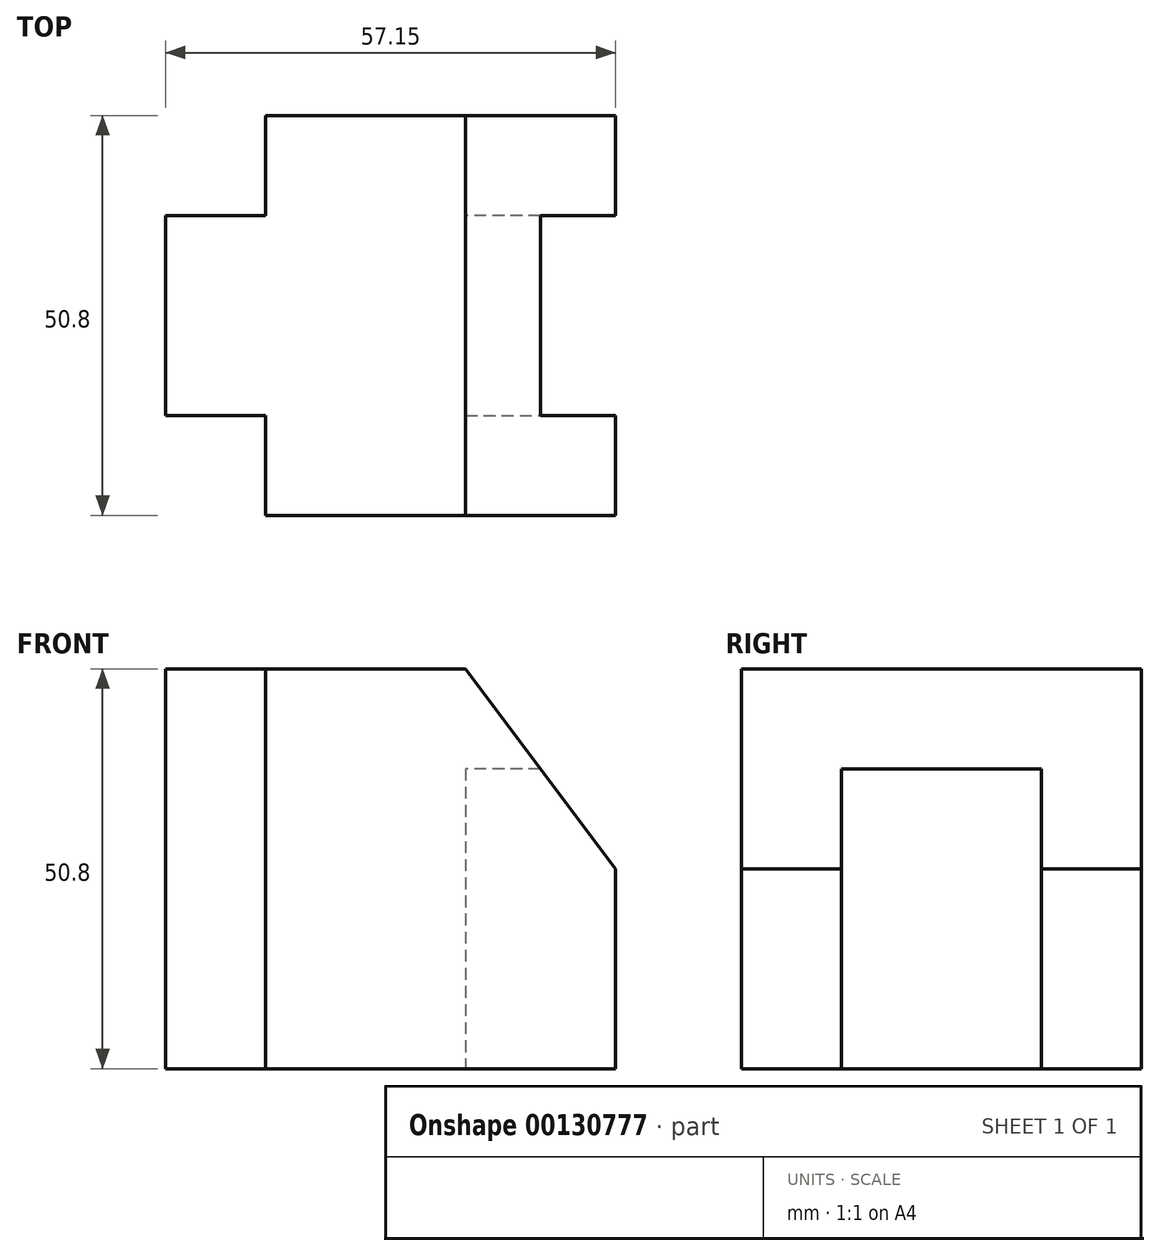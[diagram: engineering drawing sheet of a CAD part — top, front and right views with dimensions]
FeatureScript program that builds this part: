
annotation { "Feature Type Name" : "Feature", "Feature Type Description" : "" }
export const myFeature = defineFeature(function(context is Context, id is Id, definition is map)
    precondition{}
    {
        {
            var Q0;
            Q0=qCreatedBy(makeId("Top.planeOp"),FACE);
            var sketch = newSketch(context, id + "F0", { "sketchPlane" : qUnion([Q0])});
            skLineSegment(sketch, "E0", {"start": v(12.7, 0) * mm, "end": v(12.7, 12.7) * mm});
            skLineSegment(sketch, "E1", {"start": v(12.7, 12.7) * mm, "end": v(0, 12.7) * mm});
            skLineSegment(sketch, "E2", {"start": v(0, 12.7) * mm, "end": v(0, 38.1) * mm});
            skLineSegment(sketch, "E3", {"start": v(0, 38.1) * mm, "end": v(12.7, 38.1) * mm});
            skLineSegment(sketch, "E4", {"start": v(12.7, 38.1) * mm, "end": v(12.7, 50.8) * mm});
            skLineSegment(sketch, "E5", {"start": v(12.7, 50.8) * mm, "end": v(25.4, 50.8) * mm});
            skLineSegment(sketch, "E6", {"start": v(25.4, 50.8) * mm, "end": v(25.4, 0) * mm});
            skLineSegment(sketch, "E7", {"start": v(25.4, 0) * mm, "end": v(12.7, 0) * mm});
            skSolve(sketch);
        }
        {
            var Q0;
            Q0 = qSketchRegion(id + "F0", true);
            extrude(context, id + "F1", {"entities" : qUnion([Q0]), "depth" : 50.8 * mm});
        }
        {
            var Q0;
            Q0=qCreatedBy(makeId("Front.planeOp"),FACE);
            var sketch = newSketch(context, id + "F2", { "sketchPlane" : qUnion([Q0])});
            skLineSegment(sketch, "E8", {"start": v(25.4, 0) * mm, "end": v(25.4, 50.8) * mm});
            skLineSegment(sketch, "E9", {"start": v(25.4, 50.8) * mm, "end": v(38.1, 50.8) * mm});
            skLineSegment(sketch, "E10", {"start": v(38.1, 50.8) * mm, "end": v(57.15, 25.4) * mm});
            skLineSegment(sketch, "E11", {"start": v(57.15, 25.4) * mm, "end": v(57.15, 0) * mm});
            skLineSegment(sketch, "E12", {"start": v(57.15, 0) * mm, "end": v(25.4, 0) * mm});
            skSolve(sketch);
        }
        {
            var Q0;
            Q0 = qSketchRegion(id + "F2", true);
            extrude(context, id + "F3", {"entities" : qUnion([Q0]), "operationType" : NewBodyOperationType.ADD, "oppositeDirection" : true, "depth" : 50.8 * mm});
        }
        {
            var Q0;
            Q0=qCreatedBy(makeId("Top.planeOp"),FACE);
            var sketch = newSketch(context, id + "F4", { "sketchPlane" : qUnion([Q0])});
            skLineSegment(sketch, "E13", {"start": v(57.15, 38.1) * mm, "end": v(38.1, 38.1) * mm});
            skLineSegment(sketch, "E14", {"start": v(38.1, 38.1) * mm, "end": v(38.1, 12.7) * mm});
            skLineSegment(sketch, "E15", {"start": v(38.1, 12.7) * mm, "end": v(57.15, 12.7) * mm});
            skLineSegment(sketch, "E16", {"start": v(57.15, 12.7) * mm, "end": v(57.15, 38.1) * mm});
            skSolve(sketch);
        }
        {
            var Q0;
            Q0 = qSketchRegion(id + "F4", true);
            extrude(context, id + "F5", {"entities" : qUnion([Q0]), "operationType" : NewBodyOperationType.REMOVE, "depth" : 38.1 * mm});
        }
    });
